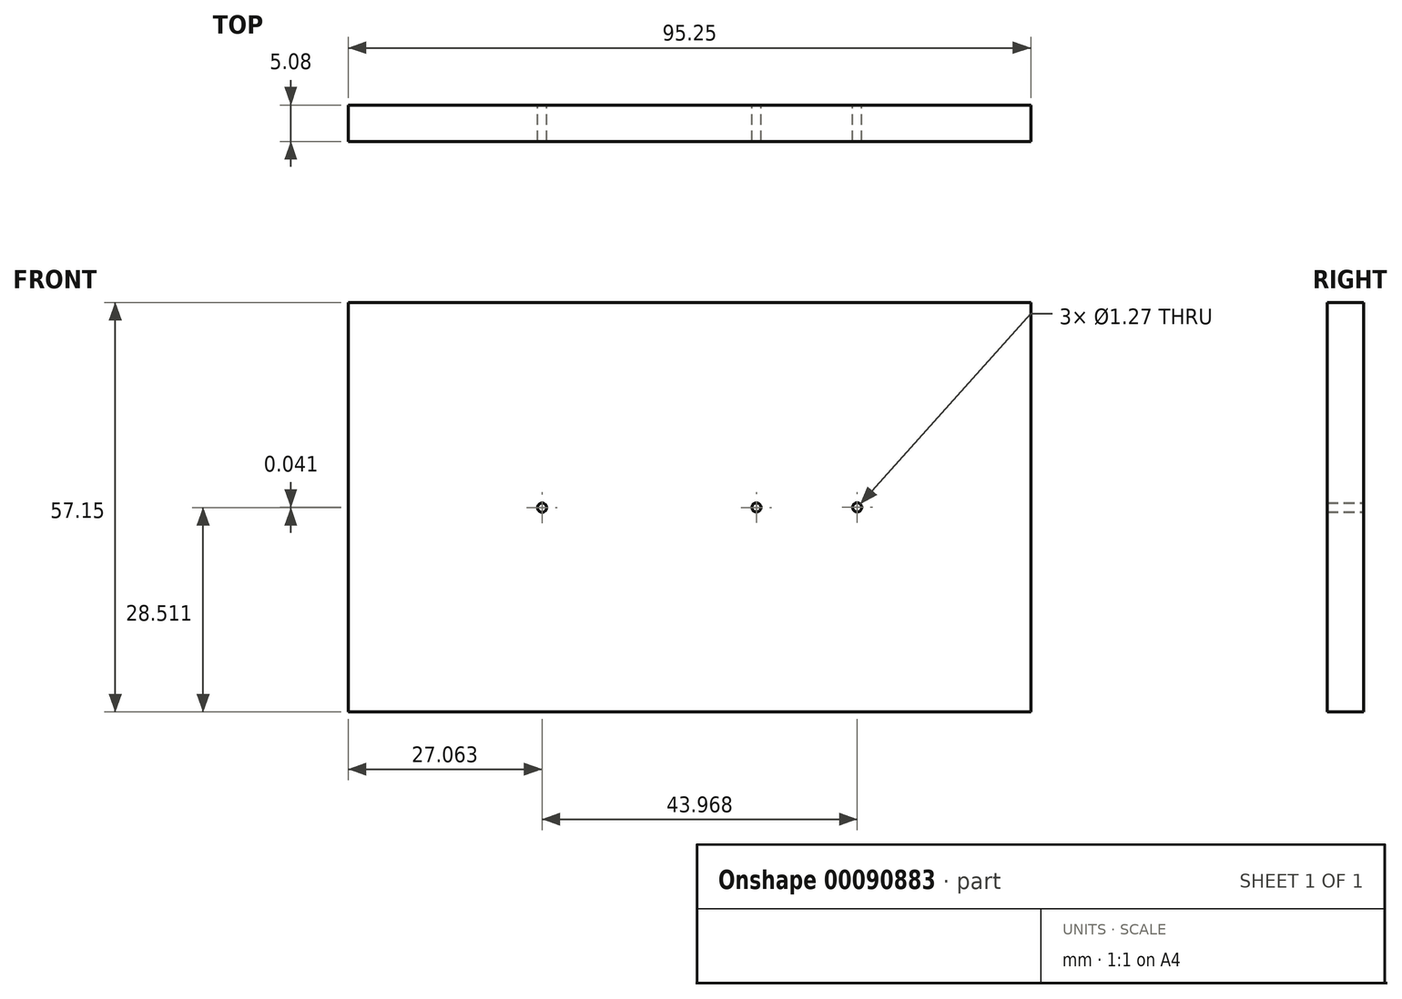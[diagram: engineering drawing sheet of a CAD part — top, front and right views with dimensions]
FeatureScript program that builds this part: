
annotation { "Feature Type Name" : "Feature", "Feature Type Description" : "" }
export const myFeature = defineFeature(function(context is Context, id is Id, definition is map)
    precondition{}
    {
        {
            var Q0;
            Q0=qCreatedBy(makeId("Front.planeOp"),FACE);
            var sketch = newSketch(context, id + "F0", { "sketchPlane" : qUnion([Q0])});
            skLineSegment(sketch, "E0.bottom", {"start": v(-48.05, 33.72) * mm, "end": v(47.2, 33.72) * mm});
            skLineSegment(sketch, "E0.top", {"start": v(-48.05, -23.43) * mm, "end": v(47.2, -23.43) * mm});
            skLineSegment(sketch, "E0.left", {"start": v(-48.05, 33.72) * mm, "end": v(-48.05, -23.43) * mm});
            skLineSegment(sketch, "E0.right", {"start": v(47.2, 33.72) * mm, "end": v(47.2, -23.43) * mm});
            skLineSegment(sketch, "E1.bottom", {"start": v(-48.05, 33.72) * mm, "end": v(-22.65, 33.72) * mm});
            skLineSegment(sketch, "E1.left", {"start": v(-48.05, 33.72) * mm, "end": v(-48.05, 13.08) * mm});
            skLineSegment(sketch, "E2.bottom", {"start": v(-48.05, 33.72) * mm, "end": v(5.92, 33.72) * mm});
            skLineSegment(sketch, "E2.left", {"start": v(-48.05, 33.72) * mm, "end": v(-48.05, 5.06) * mm});
            skLineSegment(sketch, "E3.bottom", {"start": v(-48.05, 33.72) * mm, "end": v(20.2, 33.72) * mm});
            skLineSegment(sketch, "E3.left", {"start": v(-48.05, 33.72) * mm, "end": v(-48.05, -1.2) * mm});
            skLineSegment(sketch, "E4", {"start": v(-48.05, 5.06) * mm, "end": v(47.2, 5.14) * mm});
            skCircle(sketch, "E5", {"center": v(-20.99, 5.08) * mm, "radius": 0.64 * mm});
            skCircle(sketch, "E6", {"center": v(8.92, 5.1) * mm, "radius": 0.64 * mm});
            skCircle(sketch, "E7", {"center": v(22.98, 5.12) * mm, "radius": 0.64 * mm});
            skSolve(sketch);
        }
        {
            var Q0;
            Q0 = qSketchRegion(id + "F0", true);
            extrude(context, id + "F1", {"entities" : qUnion([Q0]), "depth" : 5.08 * mm});
        }
    });
